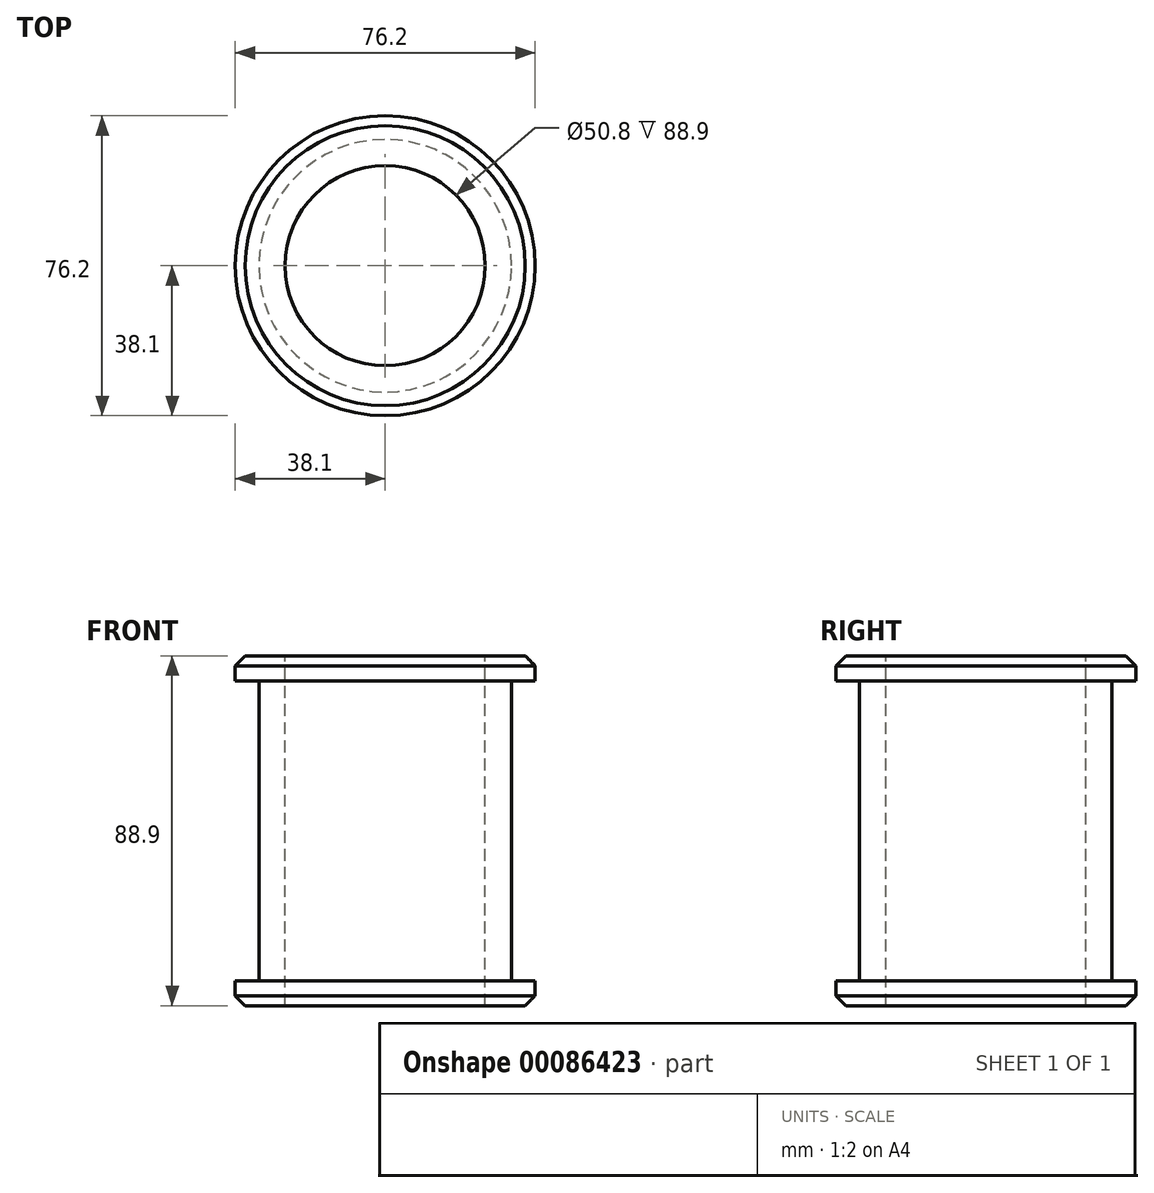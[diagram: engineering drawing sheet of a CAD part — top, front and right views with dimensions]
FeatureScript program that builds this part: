
annotation { "Feature Type Name" : "Feature", "Feature Type Description" : "" }
export const myFeature = defineFeature(function(context is Context, id is Id, definition is map)
    precondition{}
    {
        {
            var Q0;
            Q0=qCreatedBy(makeId("Front.planeOp"),FACE);
            var sketch = newSketch(context, id + "F0", { "sketchPlane" : qUnion([Q0])});
            skLineSegment(sketch, "E0.bottom", {"start": v(-32.09, 38.1) * mm, "end": v(32.09, 38.1) * mm});
            skLineSegment(sketch, "E0.top", {"start": v(-32.09, -38.1) * mm, "end": v(32.09, -38.1) * mm});
            skLineSegment(sketch, "E0.left", {"start": v(-32.09, 38.1) * mm, "end": v(-32.09, -38.1) * mm});
            skLineSegment(sketch, "E0.right", {"start": v(32.09, 38.1) * mm, "end": v(32.09, -38.1) * mm});
            skPoint(sketch, "E0.middle", {"position": v(0, 0) * mm});
            skLineSegment(sketch, "E1.bottom", {"start": v(-38.1, 38.1) * mm, "end": v(38.1, 38.1) * mm});
            skLineSegment(sketch, "E1.top", {"start": v(-38.1, 44.45) * mm, "end": v(38.1, 44.45) * mm});
            skLineSegment(sketch, "E1.left", {"start": v(-38.1, 38.1) * mm, "end": v(-38.1, 44.45) * mm});
            skLineSegment(sketch, "E1.right", {"start": v(38.1, 38.1) * mm, "end": v(38.1, 44.45) * mm});
            skPoint(sketch, "E1.middle", {"position": v(0, 41.27) * mm});
            skPoint(sketch, "E1.middle.positionSnap0", {"position": v(0, 38.1) * mm});
            skPoint(sketch, "E1.centerSnap0", {"position": v(0, 38.1) * mm});
            skLineSegment(sketch, "E2.bottom", {"start": v(-38.1, -38.1) * mm, "end": v(38.1, -38.1) * mm});
            skLineSegment(sketch, "E2.top", {"start": v(-38.1, -44.45) * mm, "end": v(38.1, -44.45) * mm});
            skLineSegment(sketch, "E2.left", {"start": v(-38.1, -38.1) * mm, "end": v(-38.1, -44.45) * mm});
            skLineSegment(sketch, "E2.right", {"start": v(38.1, -38.1) * mm, "end": v(38.1, -44.45) * mm});
            skPoint(sketch, "E2.middle", {"position": v(0, -41.28) * mm});
            skPoint(sketch, "E2.middle.positionSnap0", {"position": v(0, -38.1) * mm});
            skPoint(sketch, "E2.centerSnap0", {"position": v(0, -38.1) * mm});
            skLineSegment(sketch, "E3", {"start": v(0, 44.45) * mm, "end": v(0, -44.45) * mm});
            skSolve(sketch);
        }
        {
            var Q0;
            {var subQ0=sQuery(id+"F0.wireOp",EDGE,"E1.right");Q0=makeQuery(id+"F0.imprint","IMPRINT",FACE,{"disambiguationData":[TD([[makeQuery(id+"F0.imprint","IMPRINT",EDGE,{"derivedFrom":subQ0}),1.0]])]});}
            var Q1;
            {var subQ0=sQuery(id+"F0.wireOp",EDGE,"E0.right");Q1=makeQuery(id+"F0.imprint","IMPRINT",FACE,{"disambiguationData":[TD([[makeQuery(id+"F0.imprint","IMPRINT",EDGE,{"derivedFrom":subQ0}),-1.0]])]});}
            var Q2;
            {var subQ0=sQuery(id+"F0.wireOp",EDGE,"E2.right");Q2=makeQuery(id+"F0.imprint","IMPRINT",FACE,{"disambiguationData":[TD([[makeQuery(id+"F0.imprint","IMPRINT",EDGE,{"derivedFrom":subQ0}),-1.0]])]});}
            var Q3;
            Q3=sQuery(id+"F0.wireOp",EDGE,"E3");
            revolve(context, id + "F1", {"entities" : qUnion([Q0, Q1, Q2]), "axis" : qUnion([Q3]), "revolveType" : RevolveType.FULL});
        }
        {
            var Q0;
            Q0=makeQuery(id+"F1.opRevolve","SWEPT_FACE",FACE,{"disambiguationData":[OSD([sQuery(id+"F0.wireOp",EDGE,"E1.top")])]});
            var sketch = newSketch(context, id + "F2", { "sketchPlane" : qUnion([Q0])});
            skCircle(sketch, "E4", {"center": v(0, 0) * mm, "radius": 29.32 * mm});
            skSolve(sketch);
        }
        {
            var Q0;
            Q0=sQuery(id+"F2.wireOp",VERTEX,"E4.center");
            var Q1;
            Q1=makeQuery(id+"F1.opRevolve","SWEPT_BODY",BODY,{"disambiguationData":[OSD([sQuery(id+"F0.wireOp",EDGE,"E0.right"),sQuery(id+"F0.wireOp",EDGE,"E1.bottom"),sQuery(id+"F0.wireOp",EDGE,"E1.top"),sQuery(id+"F0.wireOp",EDGE,"E1.right"),sQuery(id+"F0.wireOp",EDGE,"E2.bottom"),sQuery(id+"F0.wireOp",EDGE,"E2.top"),sQuery(id+"F0.wireOp",EDGE,"E2.right"),sQuery(id+"F0.wireOp",EDGE,"E3")])]});
            hole(context, id + "F3", {"style" : HoleStyle.SIMPLE, "endStyle" : HoleEndStyle.THROUGH, "holeDiameter" : 50.8 * mm, "locations" : qUnion([Q0]), "scope" : qUnion([Q1]), "isTappedThrough" : true});
        }
        {
            var Q0;
            Q0=makeQuery(id+"F1.opRevolve","SWEPT_EDGE",EDGE,{"disambiguationData":[OSD([sQuery(id+"F0.wireOp",EDGE,"E1.top"),sQuery(id+"F0.wireOp",EDGE,"E1.right")])]});
            var Q1;
            Q1=makeQuery(id+"F1.opRevolve","SWEPT_EDGE",EDGE,{"disambiguationData":[OSD([sQuery(id+"F0.wireOp",EDGE,"E2.top"),sQuery(id+"F0.wireOp",EDGE,"E2.right")])]});
            chamfer(context, id + "F4", {"entities" : qUnion([Q0, Q1]), "width" : 2.54 * mm, "tangentPropagation" : true});
        }
    });
